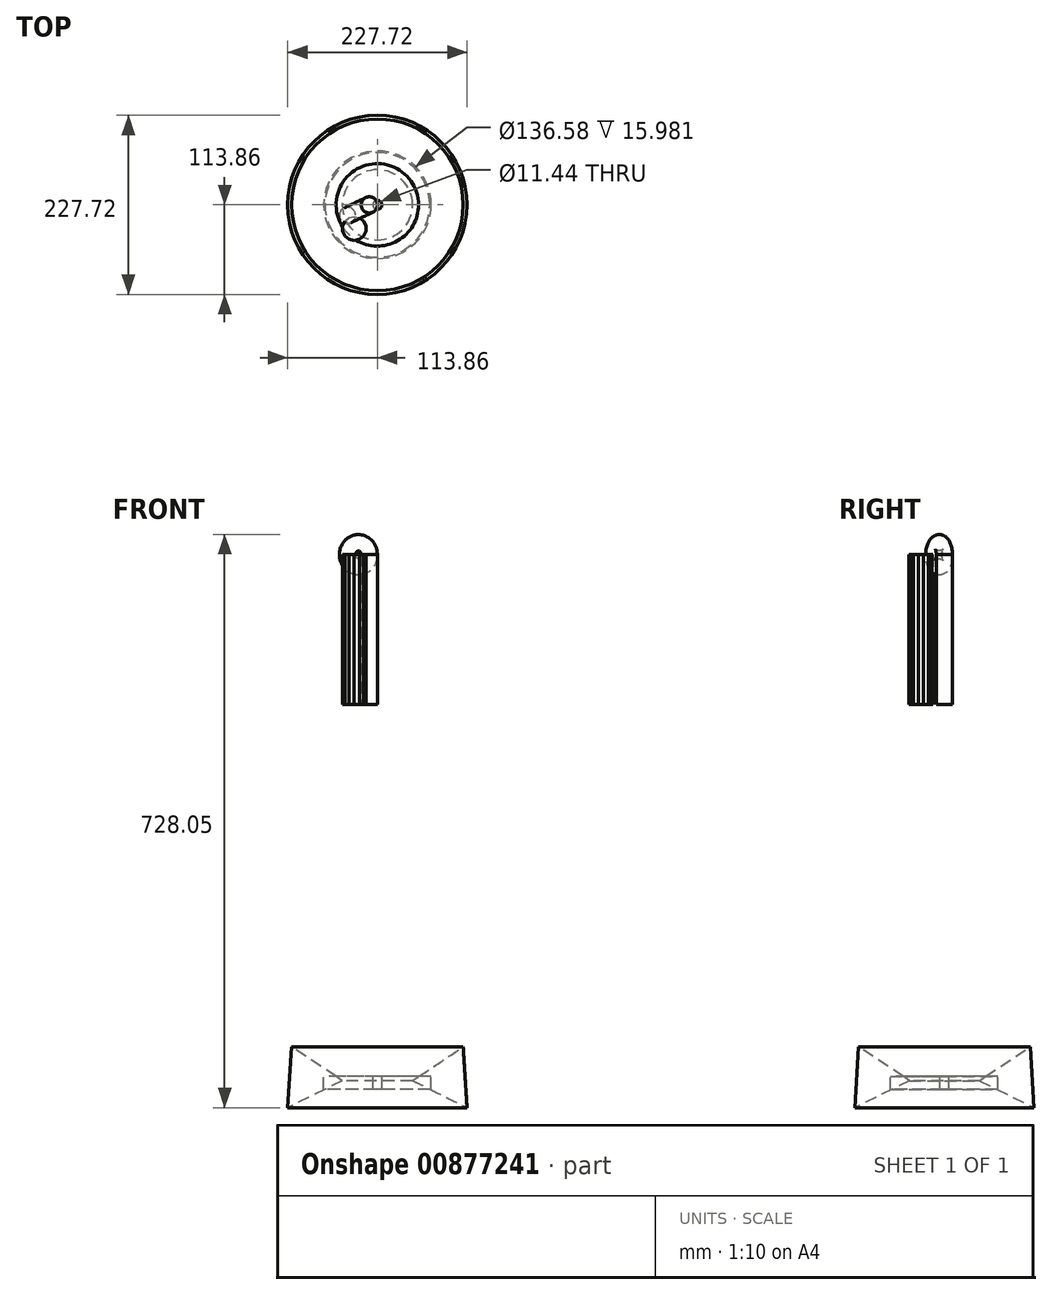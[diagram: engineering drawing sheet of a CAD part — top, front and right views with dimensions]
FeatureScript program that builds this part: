
annotation { "Feature Type Name" : "Feature", "Feature Type Description" : "" }
export const myFeature = defineFeature(function(context is Context, id is Id, definition is map)
    precondition{}
    {
        {
            var Q0;
            Q0=qCreatedBy(makeId("Front.planeOp"),FACE);
            var sketch = newSketch(context, id + "F0", { "sketchPlane" : qUnion([Q0])});
            skLineSegment(sketch, "E0", {"start": v(0, 70.96) * mm, "end": v(0, -72.9) * mm});
            skSolve(sketch);
        }
        {
            var Q0;
            Q0=qCreatedBy(makeId("Right.planeOp"),FACE);
            var sketch = newSketch(context, id + "F1", { "sketchPlane" : qUnion([Q0])});
            skLineSegment(sketch, "E1.bottom", {"start": v(-5.72, 12.12) * mm, "end": v(-68.29, 12.12) * mm});
            skLineSegment(sketch, "E1.top", {"start": v(-5.72, -3.86) * mm, "end": v(-68.29, -3.86) * mm});
            skLineSegment(sketch, "E1.left", {"start": v(-5.72, 12.12) * mm, "end": v(-5.72, -3.86) * mm});
            skLineSegment(sketch, "E1.right", {"start": v(-68.29, 12.12) * mm, "end": v(-68.29, -3.86) * mm});
            skCircle(sketch, "E2.cCircle", {"center": v(-89.17, 9.82) * mm, "radius": 22.3 * mm, "construction": true});
            skLineSegment(sketch, "E2.0", {"start": v(-44.65, 7) * mm, "end": v(-113.86, -27.33) * mm});
            skLineSegment(sketch, "E2.1", {"start": v(-113.86, -27.33) * mm, "end": v(-109, 49.78) * mm});
            skLineSegment(sketch, "E2.2", {"start": v(-109, 49.78) * mm, "end": v(-44.65, 7) * mm});
            skPoint(sketch, "E2.0.midPoint", {"position": v(-79.25, -10.16) * mm});
            skSolve(sketch);
        }
        {
            var Q0;
            {var subQ5=sQuery(id+"F1.wireOp",EDGE,"E1.left");Q0=makeQuery(id+"F1.imprint","IMPRINT",FACE,{"disambiguationData":[TD([[makeQuery(id+"F1.imprint","IMPRINT",EDGE,{"derivedFrom":subQ5}),-1.0]])]});}
            var Q1;
            {var subQ4=sQuery(id+"F1.wireOp",EDGE,"E1.right");Q1=makeQuery(id+"F1.imprint","IMPRINT",FACE,{"disambiguationData":[TD([[makeQuery(id+"F1.imprint","IMPRINT",EDGE,{"derivedFrom":subQ4}),-1.0]])]});}
            var Q2;
            Q2=sQuery(id+"F0.wireOp",EDGE,"E0");
            revolve(context, id + "F2", {"surfaceOperationType" : NewSurfaceOperationType.NEW, "entities" : qUnion([Q0, Q1]), "axis" : qUnion([Q2]), "revolveType" : RevolveType.FULL});
        }
        {
            var Q0;
            {var subQ0=sQuery(id+"F1.wireOp",EDGE,"E1.bottom");Q0=makeQuery(id+"F2.opRevolve","SWEPT_FACE",FACE,{"disambiguationData":[OSD([subQ0]),TDD([makeQuery(id+"F1.imprint","IMPRINT",EDGE,{"disambiguationData":[TD([[makeQuery(id+"F1.imprint","INTERSECT",VERTEX,{"derivedFrom":[subQ0,sQuery(id+"F1.wireOp",EDGE,"E1.left")]}),-1.0]])],"derivedFrom":subQ0})])]});}
            cPlane(context, id + "F3", {"entities" : qUnion([Q0]), "cplaneType" : CPlaneType.OFFSET, "offset" : 472.44 * mm, "width" : 152.4 * mm, "height" : 152.4 * mm});
        }
        {
            var Q0;
            Q0=qCreatedBy(id+"F3.planeOp",FACE);
            var sketch = newSketch(context, id + "F4", { "sketchPlane" : qUnion([Q0])});
            skCircle(sketch, "E3", {"center": v(-10.3, 0) * mm, "radius": 10.3 * mm});
            skLineSegment(sketch, "E4", {"start": v(-15.97, -8.6) * mm, "end": v(-29.44, -29.9) * mm});
            skCircle(sketch, "E5.cCircle", {"center": v(-29.44, -29.9) * mm, "radius": 14.86 * mm, "construction": true});
            skLineSegment(sketch, "E5.0", {"start": v(-14.58, -26.51) * mm, "end": v(-14.58, -33.3) * mm});
            skLineSegment(sketch, "E5.1", {"start": v(-14.58, -33.3) * mm, "end": v(-17.52, -39.41) * mm});
            skLineSegment(sketch, "E5.2", {"start": v(-17.52, -39.41) * mm, "end": v(-22.83, -43.64) * mm});
            skLineSegment(sketch, "E5.3", {"start": v(-22.83, -43.64) * mm, "end": v(-29.44, -45.15) * mm});
            skLineSegment(sketch, "E5.4", {"start": v(-29.44, -45.15) * mm, "end": v(-36.06, -43.64) * mm});
            skLineSegment(sketch, "E5.5", {"start": v(-36.06, -43.64) * mm, "end": v(-41.36, -39.41) * mm});
            skLineSegment(sketch, "E5.6", {"start": v(-41.36, -39.41) * mm, "end": v(-44.3, -33.3) * mm});
            skLineSegment(sketch, "E5.7", {"start": v(-44.3, -33.3) * mm, "end": v(-44.3, -26.51) * mm});
            skLineSegment(sketch, "E5.8", {"start": v(-44.3, -26.51) * mm, "end": v(-41.36, -20.4) * mm});
            skLineSegment(sketch, "E5.9", {"start": v(-41.36, -20.4) * mm, "end": v(-36.06, -16.17) * mm});
            skLineSegment(sketch, "E5.10", {"start": v(-36.06, -16.17) * mm, "end": v(-29.44, -14.66) * mm});
            skLineSegment(sketch, "E5.11", {"start": v(-29.44, -14.66) * mm, "end": v(-22.83, -16.17) * mm});
            skLineSegment(sketch, "E5.12", {"start": v(-22.83, -16.17) * mm, "end": v(-17.52, -20.4) * mm});
            skLineSegment(sketch, "E5.13", {"start": v(-17.52, -20.4) * mm, "end": v(-14.58, -26.51) * mm});
            skPoint(sketch, "E5.0.midPoint", {"position": v(-14.58, -29.9) * mm});
            skSolve(sketch);
        }
        {
            var Q0;
            Q0 = qSketchRegion(id + "F4", true);
            extrude(context, id + "F5", {"entities" : qUnion([Q0]), "depth" : 190.5 * mm, "offsetDistance" : 25.4 * mm});
        }
        {
            var Q0;
            Q0=makeQuery(id+"F5.opExtrude","CAP_FACE",FACE,{"disambiguationData":[OSD([sQuery(id+"F4.wireOp",EDGE,"E3")])],"isStart":false});
            var Q1;
            Q1=makeQuery(id+"F5.opExtrude","CAP_EDGE",EDGE,{"disambiguationData":[OSD([sQuery(id+"F4.wireOp",EDGE,"E5.13")])],"isStart":false});
            revolve(context, id + "F6", {"surfaceOperationType" : NewSurfaceOperationType.NEW, "entities" : qUnion([Q0]), "axis" : qUnion([Q1]), "revolveType" : RevolveType.FULL});
        }
    });
